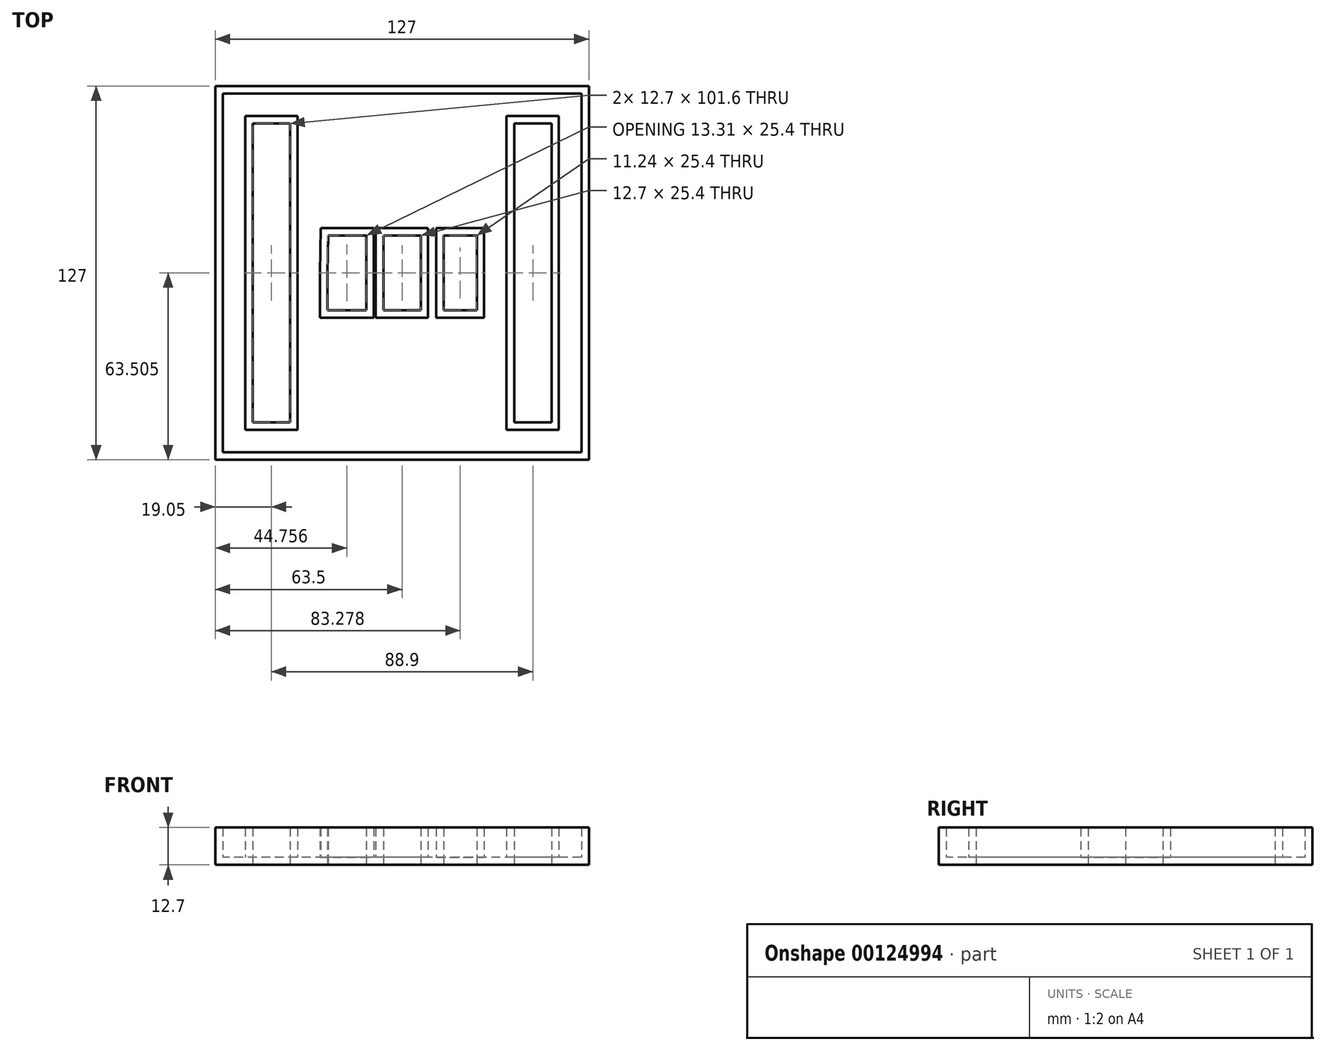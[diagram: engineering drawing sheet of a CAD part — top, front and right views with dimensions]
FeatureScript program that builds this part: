
annotation { "Feature Type Name" : "Feature", "Feature Type Description" : "" }
export const myFeature = defineFeature(function(context is Context, id is Id, definition is map)
    precondition{}
    {
        {
            var Q0;
            Q0=qCreatedBy(makeId("Top.planeOp"),FACE);
            var sketch = newSketch(context, id + "F0", { "sketchPlane" : qUnion([Q0])});
            skLineSegment(sketch, "E0", {"start": v(38.53, -43.89) * mm, "end": v(-88.47, -43.89) * mm});
            skLineSegment(sketch, "E1", {"start": v(-88.47, -43.89) * mm, "end": v(-88.47, 83.11) * mm});
            skLineSegment(sketch, "E2", {"start": v(-88.47, 83.11) * mm, "end": v(38.53, 83.11) * mm});
            skLineSegment(sketch, "E3", {"start": v(38.53, 83.11) * mm, "end": v(38.53, -43.89) * mm});
            skLineSegment(sketch, "E4", {"start": v(-75.77, 70.41) * mm, "end": v(-75.77, -31.19) * mm});
            skLineSegment(sketch, "E5", {"start": v(-75.77, -31.19) * mm, "end": v(-63.07, -31.19) * mm});
            skLineSegment(sketch, "E6", {"start": v(-63.07, -31.19) * mm, "end": v(-63.07, 70.41) * mm});
            skLineSegment(sketch, "E7", {"start": v(-63.07, 70.41) * mm, "end": v(-75.77, 70.41) * mm});
            skLineSegment(sketch, "E8", {"start": v(13.13, 70.41) * mm, "end": v(13.13, -31.19) * mm});
            skPoint(sketch, "E8.startSnap0", {"position": v(-69.42, 70.41) * mm});
            skLineSegment(sketch, "E9", {"start": v(13.13, -31.19) * mm, "end": v(25.83, -31.19) * mm});
            skLineSegment(sketch, "E10", {"start": v(25.83, -31.19) * mm, "end": v(25.83, 70.41) * mm});
            skLineSegment(sketch, "E11", {"start": v(25.83, 70.41) * mm, "end": v(13.13, 70.41) * mm});
            skLineSegment(sketch, "E12", {"start": v(-50.37, 19.61) * mm, "end": v(-50.37, 6.91) * mm});
            skPoint(sketch, "E12.startSnap0", {"position": v(-63.07, 19.61) * mm});
            skLineSegment(sketch, "E13", {"start": v(-50.37, 6.91) * mm, "end": v(-37.06, 6.91) * mm});
            skLineSegment(sketch, "E14", {"start": v(-37.06, 6.91) * mm, "end": v(-37.06, 32.31) * mm});
            skLineSegment(sketch, "E15", {"start": v(-37.06, 32.31) * mm, "end": v(-50.07, 32.31) * mm});
            skLineSegment(sketch, "E16", {"start": v(-50.07, 32.31) * mm, "end": v(-50.37, 19.61) * mm});
            skLineSegment(sketch, "E17", {"start": v(0.43, 19.61) * mm, "end": v(0.43, 32.31) * mm});
            skPoint(sketch, "E17.startSnap0", {"position": v(13.13, 19.61) * mm});
            skLineSegment(sketch, "E18", {"start": v(0.43, 32.31) * mm, "end": v(-10.81, 32.31) * mm});
            skLineSegment(sketch, "E19", {"start": v(-10.81, 32.31) * mm, "end": v(-10.81, 6.91) * mm});
            skLineSegment(sketch, "E20", {"start": v(-10.81, 6.91) * mm, "end": v(0.43, 6.91) * mm});
            skLineSegment(sketch, "E21", {"start": v(0.43, 6.91) * mm, "end": v(0.43, 19.61) * mm});
            skLineSegment(sketch, "E22", {"start": v(-24.97, 32.31) * mm, "end": v(-31.32, 32.31) * mm});
            skPoint(sketch, "E22.startSnap0", {"position": v(-24.97, 83.11) * mm});
            skLineSegment(sketch, "E23", {"start": v(-31.32, 32.31) * mm, "end": v(-31.32, 6.91) * mm});
            skLineSegment(sketch, "E24", {"start": v(-31.32, 6.91) * mm, "end": v(-18.62, 6.91) * mm});
            skLineSegment(sketch, "E25", {"start": v(-18.62, 6.91) * mm, "end": v(-18.62, 32.31) * mm});
            skLineSegment(sketch, "E26", {"start": v(-18.62, 32.31) * mm, "end": v(-24.97, 32.31) * mm});
            skSolve(sketch);
        }
        {
            var Q0;
            Q0=makeQuery(id+"F0.imprint","IMPRINT",FACE,{"disambiguationData":[TD([[makeQuery(id+"F0.imprint","IMPRINT",EDGE,{"derivedFrom":sQuery(id+"F0.wireOp",EDGE,"E0")}),-1.0]])]});
            extrude(context, id + "F1", {"entities" : qUnion([Q0]), "depth" : 12.7 * mm});
        }
        {
            var Q0;
            Q0=makeQuery(id+"F1.opExtrude","CAP_FACE",FACE,{"disambiguationData":[OSD([sQuery(id+"F0.wireOp",EDGE,"E0"),sQuery(id+"F0.wireOp",EDGE,"E1"),sQuery(id+"F0.wireOp",EDGE,"E2"),sQuery(id+"F0.wireOp",EDGE,"E3"),sQuery(id+"F0.wireOp",EDGE,"E4"),sQuery(id+"F0.wireOp",EDGE,"E5"),sQuery(id+"F0.wireOp",EDGE,"E6"),sQuery(id+"F0.wireOp",EDGE,"E7"),sQuery(id+"F0.wireOp",EDGE,"E8"),sQuery(id+"F0.wireOp",EDGE,"E9"),sQuery(id+"F0.wireOp",EDGE,"E10"),sQuery(id+"F0.wireOp",EDGE,"E11"),sQuery(id+"F0.wireOp",EDGE,"E12"),sQuery(id+"F0.wireOp",EDGE,"E13"),sQuery(id+"F0.wireOp",EDGE,"E14"),sQuery(id+"F0.wireOp",EDGE,"E15"),sQuery(id+"F0.wireOp",EDGE,"E16"),sQuery(id+"F0.wireOp",EDGE,"E17"),sQuery(id+"F0.wireOp",EDGE,"E18"),sQuery(id+"F0.wireOp",EDGE,"E19"),sQuery(id+"F0.wireOp",EDGE,"E20"),sQuery(id+"F0.wireOp",EDGE,"E21"),sQuery(id+"F0.wireOp",EDGE,"E22"),sQuery(id+"F0.wireOp",EDGE,"E23"),sQuery(id+"F0.wireOp",EDGE,"E24"),sQuery(id+"F0.wireOp",EDGE,"E25"),sQuery(id+"F0.wireOp",EDGE,"E26")])],"isStart":false});
            shell(context, id + "F2", {"entities" : qUnion([Q0]), "thickness" : 2.54 * mm});
        }
    });
